# Revit family: 859-000X-001 DN350-600
name_source: partatom
category: Pipe Accessories
units: mm (PartAtom-declared; Revit-internal decimal feet)

## family parameters
Always vertical = Yes
Cut with Voids When Loaded = No
Part Type = Valve - Breaks Into
Round Connector Dimension = Use Diameter
Shared = No
Work Plane-Based = No

## types (34) — shared parameters
10 = 10 mm  [stored 0.0328084 ft]
18 = 11 mm  [stored 0.0360892 ft]
3 = 3 mm  [stored 0.00984252 ft]
50 = 50 mm
8 = 8 mm  [stored 0.0262467 ft]
DN350_PN10 Pilot range ( 0.1 - 1) = 859-0350-00-0140003
DN350_PN10 Pilot range ( 0.6 - 6) = 859-0350-00-0140000
DN350_PN10 Pilot range ( 5 - 10) = 859-0350-00-0140001
DN350_PN16 Pilot range ( 0.1 - 1) = 859-0350-00-1140003
DN350_PN16 Pilot range ( 0.6 - 6) = 859-0350-00-1140000
DN350_PN16 Pilot range ( 10 - 16) = 859-0350-00-1140002
DN350_PN16 Pilot range ( 5 - 10) = 859-0350-00-1140001
DN400_PN10 Pilot range ( 0.1 - 1) = 859-0400-00-0140003
DN400_PN10 Pilot range ( 0.6 - 6) = 859-0400-00-0140000
DN400_PN10 Pilot range ( 5 - 10) = 859-0400-00-0140001
DN400_PN16 Pilot range ( 0.1 - 1) = 859-0400-00-1140003
DN400_PN16 Pilot range ( 0.6 - 6) = 859-0400-00-1140000
DN400_PN16 Pilot range ( 10 - 16) = 859-0400-00-1140002
DN400_PN16 Pilot range ( 5 - 10) = 859-0400-00-1140001
DN450_PN10 Pilot range ( 0.1 - 1) = 859-0450-00-0140003
DN450_PN10 Pilot range ( 0.6 - 6) = 859-0450-00-0140000
DN450_PN10 Pilot range ( 5 - 10) = 859-0450-00-0140001
DN450_PN16 Pilot range (  0.1 - 1) = 859-0450-00-1140003
DN450_PN16 Pilot range ( 10 - 16) = 859-0450-00-1140002
DN450_PN16 Pilot range ( 5 - 10) = 859-0450-00-1140001
DN500_PN10 Pilot range ( 0.1 - 1) = 859-0500-00-0140003
DN500_PN10 Pilot range ( 0.6 - 6) = 859-0500-00-0140000
DN500_PN10 Pilot range ( 5 - 10) = 859-0500-00-0140001
DN500_PN16 Pilot range ( 0.1 - 1) = 859-0500-00-1140003
DN500_PN16 Pilot range ( 0.6 - 6) = 859-0500-00-1140000
DN500_PN16 Pilot range ( 10 - 16) = 859-0500-00-1140002
DN500_PN16 Pilot range ( 5 - 10) = 859-0500-00-1140001
DN600_PN10 Pilot range ( 0.1 - 1) = 859-0600-00-0140003
DN600_PN10 Pilot range ( 0.6 - 6) = 859-0600-00-0140000
DN600_PN10 Pilot range ( 5 - 10) = 859-0600-00-0140001
DN600_PN16 Pilot range ( 0.1 - 1) = 859-0600-00-1140003
DN600_PN16 Pilot range ( 0.6 - 6) = 859-0600-00-1140000
DN600_PN16 Pilot range ( 10 - 16) = 859-0600-00-1140002
DN600_PN16 Pilot range ( 5 - 10) = 859-0600-00-1140001
Description_ = AVK CONTROL VALVE, PRESSURE REDUCING, PN10/16
Search_table = 859-000X-001 DN350-600
URL_product_pages = https://www.avkvalves.com
zero-valued in all types: 0, Default Elevation, Nut_Dim_T

## per-type parameters (varying)
- DN350_PN10 Pilot range ( 0.6 - 6): Actuator_L=136 mm; Actuator_L1=122 mm; Actuator_d=49 mm; Body_H=282 mm; Body_Rib_L=118 mm; Bolt_Dia=33 mm; Bonnet_D=141 mm; Bonnet_D1=282 mm; Bonnet_R=296 mm; Bonnet_dim1=197 mm; Bonnet_dim1_H=41 mm; Bonnet_dim1_H1=400 mm; Bonnet_dim2=99 mm; Bonnet_dim3=74 mm; Bore=175 mm; Bore1=210 mm; Bore2=200 mm; Bore22=220 mm; Centre_D=70 mm; Centre_D1=56 mm; Centre_nut=53 mm; Control_dim1=19 mm  [stored 0.062336 ft]; Control_dim2=89 mm; Control_dim3=9 mm  [stored 0.0295276 ft]; Control_dim4=254 mm; Control_dim5=25 mm  [stored 0.082021 ft]; Control_dim6=30 mm  [stored 0.0984252 ft]; Control_dim7=40 mm  [stored 0.131234 ft]; D=235 mm; DN=350 mm; FL_T=25 mm  [stored 0.082021 ft]; H3=794 mm; H33=48 mm; H4=96 mm; L=980 mm; L3=326 mm; Nut_Dim1=42 mm; Nut_Dim2=7 mm  [stored 0.0229659 ft]; Nut_T=16 mm; Raised_R=24 mm  [stored 0.0787402 ft]; Raised_dis=4 mm  [stored 0.0131234 ft]; Sweep_R=19 mm  [stored 0.062336 ft]; Thickness=15 mm  [stored 0.0492126 ft]; Thickness1=18 mm  [stored 0.0590551 ft]; W=290 mm; W1=302 mm; W11=249 mm; W2=302 mm; W22=196 mm; bore2=200 mm; centre=273 mm; dim1=60 mm; dim2=151 mm; nut_dim=141 mm; sweep=30 mm  [stored 0.0984252 ft]; sweep/2=6 mm  [stored 0.019685 ft]; sweep1=13 mm  [stored 0.0426509 ft]; sweep_D=25 mm  [stored 0.082021 ft]; sweep_H=363 mm; sweep_H1=57 mm; sweep_box1=28 mm  [stored 0.0918635 ft]; sweep_box2=16 mm
- DN350_PN10 Pilot range ( 5 - 10): Actuator_L=136 mm; Actuator_L1=122 mm; Actuator_d=49 mm; Body_H=282 mm; Body_Rib_L=118 mm; Bolt_Dia=33 mm; Bonnet_D=141 mm; Bonnet_D1=282 mm; Bonnet_R=296 mm; Bonnet_dim1=197 mm; Bonnet_dim1_H=41 mm; Bonnet_dim1_H1=400 mm; Bonnet_dim2=99 mm; Bonnet_dim3=74 mm; Bore=175 mm; Bore1=210 mm; Bore2=200 mm; Bore22=220 mm; Centre_D=70 mm; Centre_D1=56 mm; Centre_nut=53 mm; Control_dim1=19 mm  [stored 0.062336 ft]; Control_dim2=89 mm; Control_dim3=9 mm  [stored 0.0295276 ft]; Control_dim4=254 mm; Control_dim5=25 mm  [stored 0.082021 ft]; Control_dim6=30 mm  [stored 0.0984252 ft]; Control_dim7=40 mm  [stored 0.131234 ft]; D=235 mm; DN=350 mm; FL_T=25 mm  [stored 0.082021 ft]; H3=794 mm; H33=48 mm; H4=96 mm; L=980 mm; L3=326 mm; Nut_Dim1=42 mm; Nut_Dim2=7 mm  [stored 0.0229659 ft]; Nut_T=16 mm; Raised_R=24 mm  [stored 0.0787402 ft]; Raised_dis=4 mm  [stored 0.0131234 ft]; Sweep_R=19 mm  [stored 0.062336 ft]; Thickness=15 mm  [stored 0.0492126 ft]; Thickness1=18 mm  [stored 0.0590551 ft]; W=290 mm; W1=302 mm; W11=249 mm; W2=302 mm; W22=196 mm; bore2=200 mm; centre=273 mm; dim1=60 mm; dim2=151 mm; nut_dim=141 mm; sweep=30 mm  [stored 0.0984252 ft]; sweep/2=6 mm  [stored 0.019685 ft]; sweep1=13 mm  [stored 0.0426509 ft]; sweep_D=25 mm  [stored 0.082021 ft]; sweep_H=363 mm; sweep_H1=57 mm; sweep_box1=28 mm  [stored 0.0918635 ft]; sweep_box2=16 mm
- DN350_PN10 Pilot range ( 0.1 - 1): Actuator_L=136 mm; Actuator_L1=122 mm; Actuator_d=49 mm; Body_H=282 mm; Body_Rib_L=118 mm; Bolt_Dia=33 mm; Bonnet_D=141 mm; Bonnet_D1=282 mm; Bonnet_R=296 mm; Bonnet_dim1=197 mm; Bonnet_dim1_H=41 mm; Bonnet_dim1_H1=400 mm; Bonnet_dim2=99 mm; Bonnet_dim3=74 mm; Bore=175 mm; Bore1=210 mm; Bore2=200 mm; Bore22=220 mm; Centre_D=70 mm; Centre_D1=56 mm; Centre_nut=53 mm; Control_dim1=19 mm  [stored 0.062336 ft]; Control_dim2=89 mm; Control_dim3=9 mm  [stored 0.0295276 ft]; Control_dim4=254 mm; Control_dim5=25 mm  [stored 0.082021 ft]; Control_dim6=30 mm  [stored 0.0984252 ft]; Control_dim7=40 mm  [stored 0.131234 ft]; D=235 mm; DN=350 mm; FL_T=25 mm  [stored 0.082021 ft]; H3=794 mm; H33=48 mm; H4=96 mm; L=980 mm; L3=326 mm; Nut_Dim1=42 mm; Nut_Dim2=7 mm  [stored 0.0229659 ft]; Nut_T=16 mm; Raised_R=24 mm  [stored 0.0787402 ft]; Raised_dis=4 mm  [stored 0.0131234 ft]; Sweep_R=19 mm  [stored 0.062336 ft]; Thickness=15 mm  [stored 0.0492126 ft]; Thickness1=18 mm  [stored 0.0590551 ft]; W=290 mm; W1=302 mm; W11=249 mm; W2=302 mm; W22=196 mm; bore2=200 mm; centre=273 mm; dim1=60 mm; dim2=151 mm; nut_dim=141 mm; sweep=30 mm  [stored 0.0984252 ft]; sweep/2=6 mm  [stored 0.019685 ft]; sweep1=13 mm  [stored 0.0426509 ft]; sweep_D=25 mm  [stored 0.082021 ft]; sweep_H=363 mm; sweep_H1=57 mm; sweep_box1=28 mm  [stored 0.0918635 ft]; sweep_box2=16 mm
- DN350_PN16 Pilot range ( 0.6 - 6): Actuator_L=136 mm; Actuator_L1=122 mm; Actuator_d=49 mm; Body_H=282 mm; Body_Rib_L=118 mm; Bolt_Dia=33 mm; Bonnet_D=141 mm; Bonnet_D1=282 mm; Bonnet_R=296 mm; Bonnet_dim1=197 mm; Bonnet_dim1_H=41 mm; Bonnet_dim1_H1=400 mm; Bonnet_dim2=99 mm; Bonnet_dim3=74 mm; Bore=175 mm; Bore1=210 mm; Bore2=200 mm; Bore22=220 mm; Centre_D=70 mm; Centre_D1=56 mm; Centre_nut=53 mm; Control_dim1=19 mm  [stored 0.062336 ft]; Control_dim2=89 mm; Control_dim3=9 mm  [stored 0.0295276 ft]; Control_dim4=254 mm; Control_dim5=25 mm  [stored 0.082021 ft]; Control_dim6=30 mm  [stored 0.0984252 ft]; Control_dim7=40 mm  [stored 0.131234 ft]; D=235 mm; DN=350 mm; FL_T=25 mm  [stored 0.082021 ft]; H3=794 mm; H33=48 mm; H4=96 mm; L=980 mm; L3=326 mm; Nut_Dim1=42 mm; Nut_Dim2=7 mm  [stored 0.0229659 ft]; Nut_T=16 mm; Raised_R=24 mm  [stored 0.0787402 ft]; Raised_dis=4 mm  [stored 0.0131234 ft]; Sweep_R=19 mm  [stored 0.062336 ft]; Thickness=15 mm  [stored 0.0492126 ft]; Thickness1=18 mm  [stored 0.0590551 ft]; W=290 mm; W1=302 mm; W11=249 mm; W2=302 mm; W22=196 mm; bore2=200 mm; centre=273 mm; dim1=60 mm; dim2=151 mm; nut_dim=141 mm; sweep=30 mm  [stored 0.0984252 ft]; sweep/2=6 mm  [stored 0.019685 ft]; sweep1=13 mm  [stored 0.0426509 ft]; sweep_D=25 mm  [stored 0.082021 ft]; sweep_H=363 mm; sweep_H1=57 mm; sweep_box1=28 mm  [stored 0.0918635 ft]; sweep_box2=16 mm
- DN350_PN16 Pilot range ( 5 - 10): Actuator_L=136 mm; Actuator_L1=122 mm; Actuator_d=49 mm; Body_H=282 mm; Body_Rib_L=118 mm; Bolt_Dia=33 mm; Bonnet_D=141 mm; Bonnet_D1=282 mm; Bonnet_R=296 mm; Bonnet_dim1=197 mm; Bonnet_dim1_H=41 mm; Bonnet_dim1_H1=400 mm; Bonnet_dim2=99 mm; Bonnet_dim3=74 mm; Bore=175 mm; Bore1=210 mm; Bore2=200 mm; Bore22=220 mm; Centre_D=70 mm; Centre_D1=56 mm; Centre_nut=53 mm; Control_dim1=19 mm  [stored 0.062336 ft]; Control_dim2=89 mm; Control_dim3=9 mm  [stored 0.0295276 ft]; Control_dim4=254 mm; Control_dim5=25 mm  [stored 0.082021 ft]; Control_dim6=30 mm  [stored 0.0984252 ft]; Control_dim7=40 mm  [stored 0.131234 ft]; D=235 mm; DN=350 mm; FL_T=25 mm  [stored 0.082021 ft]; H3=794 mm; H33=48 mm; H4=96 mm; L=980 mm; L3=326 mm; Nut_Dim1=42 mm; Nut_Dim2=7 mm  [stored 0.0229659 ft]; Nut_T=16 mm; Raised_R=24 mm  [stored 0.0787402 ft]; Raised_dis=4 mm  [stored 0.0131234 ft]; Sweep_R=19 mm  [stored 0.062336 ft]; Thickness=15 mm  [stored 0.0492126 ft]; Thickness1=18 mm  [stored 0.0590551 ft]; W=290 mm; W1=302 mm; W11=249 mm; W2=302 mm; W22=196 mm; bore2=200 mm; centre=273 mm; dim1=60 mm; dim2=151 mm; nut_dim=141 mm; sweep=30 mm  [stored 0.0984252 ft]; sweep/2=6 mm  [stored 0.019685 ft]; sweep1=13 mm  [stored 0.0426509 ft]; sweep_D=25 mm  [stored 0.082021 ft]; sweep_H=363 mm; sweep_H1=57 mm; sweep_box1=28 mm  [stored 0.0918635 ft]; sweep_box2=16 mm
- DN350_PN16 Pilot range ( 10 - 16): Actuator_L=136 mm; Actuator_L1=122 mm; Actuator_d=49 mm; Body_H=282 mm; Body_Rib_L=118 mm; Bolt_Dia=33 mm; Bonnet_D=141 mm; Bonnet_D1=282 mm; Bonnet_R=296 mm; Bonnet_dim1=197 mm; Bonnet_dim1_H=41 mm; Bonnet_dim1_H1=400 mm; Bonnet_dim2=99 mm; Bonnet_dim3=74 mm; Bore=175 mm; Bore1=210 mm; Bore2=200 mm; Bore22=220 mm; Centre_D=70 mm; Centre_D1=56 mm; Centre_nut=53 mm; Control_dim1=19 mm  [stored 0.062336 ft]; Control_dim2=89 mm; Control_dim3=9 mm  [stored 0.0295276 ft]; Control_dim4=254 mm; Control_dim5=25 mm  [stored 0.082021 ft]; Control_dim6=30 mm  [stored 0.0984252 ft]; Control_dim7=40 mm  [stored 0.131234 ft]; D=235 mm; DN=350 mm; FL_T=25 mm  [stored 0.082021 ft]; H3=794 mm; H33=48 mm; H4=96 mm; L=980 mm; L3=326 mm; Nut_Dim1=42 mm; Nut_Dim2=7 mm  [stored 0.0229659 ft]; Nut_T=16 mm; Raised_R=24 mm  [stored 0.0787402 ft]; Raised_dis=4 mm  [stored 0.0131234 ft]; Sweep_R=19 mm  [stored 0.062336 ft]; Thickness=15 mm  [stored 0.0492126 ft]; Thickness1=18 mm  [stored 0.0590551 ft]; W=290 mm; W1=302 mm; W11=249 mm; W2=302 mm; W22=196 mm; bore2=200 mm; centre=273 mm; dim1=60 mm; dim2=151 mm; nut_dim=141 mm; sweep=30 mm  [stored 0.0984252 ft]; sweep/2=6 mm  [stored 0.019685 ft]; sweep1=13 mm  [stored 0.0426509 ft]; sweep_D=25 mm  [stored 0.082021 ft]; sweep_H=363 mm; sweep_H1=57 mm; sweep_box1=28 mm  [stored 0.0918635 ft]; sweep_box2=16 mm
- DN350_PN16 Pilot range ( 0.1 - 1): Actuator_L=136 mm; Actuator_L1=122 mm; Actuator_d=49 mm; Body_H=282 mm; Body_Rib_L=118 mm; Bolt_Dia=33 mm; Bonnet_D=141 mm; Bonnet_D1=282 mm; Bonnet_R=296 mm; Bonnet_dim1=197 mm; Bonnet_dim1_H=41 mm; Bonnet_dim1_H1=400 mm; Bonnet_dim2=99 mm; Bonnet_dim3=74 mm; Bore=175 mm; Bore1=210 mm; Bore2=200 mm; Bore22=220 mm; Centre_D=70 mm; Centre_D1=56 mm; Centre_nut=53 mm; Control_dim1=19 mm  [stored 0.062336 ft]; Control_dim2=89 mm; Control_dim3=9 mm  [stored 0.0295276 ft]; Control_dim4=254 mm; Control_dim5=25 mm  [stored 0.082021 ft]; Control_dim6=30 mm  [stored 0.0984252 ft]; Control_dim7=40 mm  [stored 0.131234 ft]; D=235 mm; DN=350 mm; FL_T=25 mm  [stored 0.082021 ft]; H3=794 mm; H33=48 mm; H4=96 mm; L=980 mm; L3=326 mm; Nut_Dim1=42 mm; Nut_Dim2=7 mm  [stored 0.0229659 ft]; Nut_T=16 mm; Raised_R=24 mm  [stored 0.0787402 ft]; Raised_dis=4 mm  [stored 0.0131234 ft]; Sweep_R=19 mm  [stored 0.062336 ft]; Thickness=15 mm  [stored 0.0492126 ft]; Thickness1=18 mm  [stored 0.0590551 ft]; W=290 mm; W1=302 mm; W11=249 mm; W2=302 mm; W22=196 mm; bore2=200 mm; centre=273 mm; dim1=60 mm; dim2=151 mm; nut_dim=141 mm; sweep=30 mm  [stored 0.0984252 ft]; sweep/2=6 mm  [stored 0.019685 ft]; sweep1=13 mm  [stored 0.0426509 ft]; sweep_D=25 mm  [stored 0.082021 ft]; sweep_H=363 mm; sweep_H1=57 mm; sweep_box1=28 mm  [stored 0.0918635 ft]; sweep_box2=16 mm
- DN400_PN10 Pilot range ( 0.6 - 6): Actuator_L=154 mm; Actuator_L1=139 mm; Actuator_d=54 mm; Body_H=315 mm; Body_Rib_L=131 mm; Bolt_Dia=39 mm  [stored 0.127953 ft]; Bonnet_D=158 mm; Bonnet_D1=315 mm; Bonnet_R=331 mm; Bonnet_dim1=221 mm; Bonnet_dim1_H=53 mm; Bonnet_dim1_H1=463 mm; Bonnet_dim2=110 mm; Bonnet_dim3=83 mm; Bore=200 mm; Bore1=240 mm; Bore2=223 mm; Bore22=245 mm; Centre_D=80 mm; Centre_D1=64 mm; Centre_nut=60 mm; Control_dim1=21 mm  [stored 0.0688976 ft]; Control_dim2=99 mm; Control_dim3=10 mm  [stored 0.0328084 ft]; Control_dim4=284 mm; Control_dim5=28 mm  [stored 0.0918635 ft]; Control_dim6=33 mm; Control_dim7=45 mm  [stored 0.147638 ft]; D=263 mm; DN=400 mm; FL_T=25 mm  [stored 0.082021 ft]; H3=910 mm; H33=55 mm; H4=111 mm; L=1100 mm; L3=364 mm; Nut_Dim1=51 mm; Nut_Dim2=8 mm  [stored 0.0262467 ft]; Nut_T=16 mm; Raised_R=25 mm  [stored 0.082021 ft]; Raised_dis=4 mm  [stored 0.0131234 ft]; Sweep_R=23 mm; Thickness=15 mm  [stored 0.0492126 ft]; Thickness1=18 mm  [stored 0.0590551 ft]; W=328 mm; W1=343 mm; W11=281 mm; W2=343 mm; W22=223 mm; bore2=223 mm; centre=312 mm; dim1=69 mm; dim2=171 mm; nut_dim=158 mm; sweep=36 mm  [stored 0.11811 ft]; sweep/2=8 mm  [stored 0.0262467 ft]; sweep1=15 mm  [stored 0.0492126 ft]; sweep_D=30 mm  [stored 0.0984252 ft]; sweep_H=421 mm; sweep_H1=74 mm; sweep_box1=32 mm  [stored 0.104987 ft]; sweep_box2=20 mm  [stored 0.0656168 ft]
- DN400_PN10 Pilot range ( 5 - 10): Actuator_L=154 mm; Actuator_L1=139 mm; Actuator_d=54 mm; Body_H=315 mm; Body_Rib_L=131 mm; Bolt_Dia=39 mm  [stored 0.127953 ft]; Bonnet_D=158 mm; Bonnet_D1=315 mm; Bonnet_R=331 mm; Bonnet_dim1=221 mm; Bonnet_dim1_H=53 mm; Bonnet_dim1_H1=463 mm; Bonnet_dim2=110 mm; Bonnet_dim3=83 mm; Bore=200 mm; Bore1=240 mm; Bore2=223 mm; Bore22=245 mm; Centre_D=80 mm; Centre_D1=64 mm; Centre_nut=60 mm; Control_dim1=21 mm  [stored 0.0688976 ft]; Control_dim2=99 mm; Control_dim3=10 mm  [stored 0.0328084 ft]; Control_dim4=284 mm; Control_dim5=28 mm  [stored 0.0918635 ft]; Control_dim6=33 mm; Control_dim7=45 mm  [stored 0.147638 ft]; D=263 mm; DN=400 mm; FL_T=25 mm  [stored 0.082021 ft]; H3=910 mm; H33=55 mm; H4=111 mm; L=1100 mm; L3=364 mm; Nut_Dim1=51 mm; Nut_Dim2=8 mm  [stored 0.0262467 ft]; Nut_T=16 mm; Raised_R=25 mm  [stored 0.082021 ft]; Raised_dis=4 mm  [stored 0.0131234 ft]; Sweep_R=23 mm; Thickness=15 mm  [stored 0.0492126 ft]; Thickness1=18 mm  [stored 0.0590551 ft]; W=328 mm; W1=343 mm; W11=281 mm; W2=343 mm; W22=223 mm; bore2=223 mm; centre=312 mm; dim1=69 mm; dim2=171 mm; nut_dim=158 mm; sweep=36 mm  [stored 0.11811 ft]; sweep/2=8 mm  [stored 0.0262467 ft]; sweep1=15 mm  [stored 0.0492126 ft]; sweep_D=30 mm  [stored 0.0984252 ft]; sweep_H=421 mm; sweep_H1=74 mm; sweep_box1=32 mm  [stored 0.104987 ft]; sweep_box2=20 mm  [stored 0.0656168 ft]
- DN400_PN10 Pilot range ( 0.1 - 1): Actuator_L=154 mm; Actuator_L1=139 mm; Actuator_d=54 mm; Body_H=315 mm; Body_Rib_L=131 mm; Bolt_Dia=39 mm  [stored 0.127953 ft]; Bonnet_D=158 mm; Bonnet_D1=315 mm; Bonnet_R=331 mm; Bonnet_dim1=221 mm; Bonnet_dim1_H=53 mm; Bonnet_dim1_H1=463 mm; Bonnet_dim2=110 mm; Bonnet_dim3=83 mm; Bore=200 mm; Bore1=240 mm; Bore2=223 mm; Bore22=245 mm; Centre_D=80 mm; Centre_D1=64 mm; Centre_nut=60 mm; Control_dim1=21 mm  [stored 0.0688976 ft]; Control_dim2=99 mm; Control_dim3=10 mm  [stored 0.0328084 ft]; Control_dim4=284 mm; Control_dim5=28 mm  [stored 0.0918635 ft]; Control_dim6=33 mm; Control_dim7=45 mm  [stored 0.147638 ft]; D=263 mm; DN=400 mm; FL_T=25 mm  [stored 0.082021 ft]; H3=910 mm; H33=55 mm; H4=111 mm; L=1100 mm; L3=364 mm; Nut_Dim1=51 mm; Nut_Dim2=8 mm  [stored 0.0262467 ft]; Nut_T=16 mm; Raised_R=25 mm  [stored 0.082021 ft]; Raised_dis=4 mm  [stored 0.0131234 ft]; Sweep_R=23 mm; Thickness=15 mm  [stored 0.0492126 ft]; Thickness1=18 mm  [stored 0.0590551 ft]; W=328 mm; W1=343 mm; W11=281 mm; W2=343 mm; W22=223 mm; bore2=223 mm; centre=312 mm; dim1=69 mm; dim2=171 mm; nut_dim=158 mm; sweep=36 mm  [stored 0.11811 ft]; sweep/2=8 mm  [stored 0.0262467 ft]; sweep1=15 mm  [stored 0.0492126 ft]; sweep_D=30 mm  [stored 0.0984252 ft]; sweep_H=421 mm; sweep_H1=74 mm; sweep_box1=32 mm  [stored 0.104987 ft]; sweep_box2=20 mm  [stored 0.0656168 ft]
- DN400_PN16 Pilot range ( 0.6 - 6): Actuator_L=154 mm; Actuator_L1=139 mm; Actuator_d=54 mm; Body_H=315 mm; Body_Rib_L=131 mm; Bolt_Dia=39 mm  [stored 0.127953 ft]; Bonnet_D=158 mm; Bonnet_D1=315 mm; Bonnet_R=331 mm; Bonnet_dim1=221 mm; Bonnet_dim1_H=53 mm; Bonnet_dim1_H1=463 mm; Bonnet_dim2=110 mm; Bonnet_dim3=83 mm; Bore=200 mm; Bore1=240 mm; Bore2=223 mm; Bore22=245 mm; Centre_D=80 mm; Centre_D1=64 mm; Centre_nut=60 mm; Control_dim1=21 mm  [stored 0.0688976 ft]; Control_dim2=99 mm; Control_dim3=10 mm  [stored 0.0328084 ft]; Control_dim4=284 mm; Control_dim5=28 mm  [stored 0.0918635 ft]; Control_dim6=33 mm; Control_dim7=45 mm  [stored 0.147638 ft]; D=263 mm; DN=400 mm; FL_T=25 mm  [stored 0.082021 ft]; H3=910 mm; H33=55 mm; H4=111 mm; L=1100 mm; L3=364 mm; Nut_Dim1=51 mm; Nut_Dim2=8 mm  [stored 0.0262467 ft]; Nut_T=16 mm; Raised_R=25 mm  [stored 0.082021 ft]; Raised_dis=4 mm  [stored 0.0131234 ft]; Sweep_R=23 mm; Thickness=15 mm  [stored 0.0492126 ft]; Thickness1=18 mm  [stored 0.0590551 ft]; W=328 mm; W1=343 mm; W11=281 mm; W2=343 mm; W22=223 mm; bore2=223 mm; centre=312 mm; dim1=69 mm; dim2=171 mm; nut_dim=158 mm; sweep=36 mm  [stored 0.11811 ft]; sweep/2=8 mm  [stored 0.0262467 ft]; sweep1=15 mm  [stored 0.0492126 ft]; sweep_D=30 mm  [stored 0.0984252 ft]; sweep_H=421 mm; sweep_H1=74 mm; sweep_box1=32 mm  [stored 0.104987 ft]; sweep_box2=20 mm  [stored 0.0656168 ft]
- DN400_PN16 Pilot range ( 5 - 10): Actuator_L=154 mm; Actuator_L1=139 mm; Actuator_d=54 mm; Body_H=315 mm; Body_Rib_L=131 mm; Bolt_Dia=39 mm  [stored 0.127953 ft]; Bonnet_D=158 mm; Bonnet_D1=315 mm; Bonnet_R=331 mm; Bonnet_dim1=221 mm; Bonnet_dim1_H=53 mm; Bonnet_dim1_H1=463 mm; Bonnet_dim2=110 mm; Bonnet_dim3=83 mm; Bore=200 mm; Bore1=240 mm; Bore2=223 mm; Bore22=245 mm; Centre_D=80 mm; Centre_D1=64 mm; Centre_nut=60 mm; Control_dim1=21 mm  [stored 0.0688976 ft]; Control_dim2=99 mm; Control_dim3=10 mm  [stored 0.0328084 ft]; Control_dim4=284 mm; Control_dim5=28 mm  [stored 0.0918635 ft]; Control_dim6=33 mm; Control_dim7=45 mm  [stored 0.147638 ft]; D=263 mm; DN=400 mm; FL_T=25 mm  [stored 0.082021 ft]; H3=910 mm; H33=55 mm; H4=111 mm; L=1100 mm; L3=364 mm; Nut_Dim1=51 mm; Nut_Dim2=8 mm  [stored 0.0262467 ft]; Nut_T=16 mm; Raised_R=25 mm  [stored 0.082021 ft]; Raised_dis=4 mm  [stored 0.0131234 ft]; Sweep_R=23 mm; Thickness=15 mm  [stored 0.0492126 ft]; Thickness1=18 mm  [stored 0.0590551 ft]; W=328 mm; W1=343 mm; W11=281 mm; W2=343 mm; W22=223 mm; bore2=223 mm; centre=312 mm; dim1=69 mm; dim2=171 mm; nut_dim=158 mm; sweep=36 mm  [stored 0.11811 ft]; sweep/2=8 mm  [stored 0.0262467 ft]; sweep1=15 mm  [stored 0.0492126 ft]; sweep_D=30 mm  [stored 0.0984252 ft]; sweep_H=421 mm; sweep_H1=74 mm; sweep_box1=32 mm  [stored 0.104987 ft]; sweep_box2=20 mm  [stored 0.0656168 ft]
- DN400_PN16 Pilot range ( 10 - 16): Actuator_L=154 mm; Actuator_L1=139 mm; Actuator_d=54 mm; Body_H=315 mm; Body_Rib_L=131 mm; Bolt_Dia=39 mm  [stored 0.127953 ft]; Bonnet_D=158 mm; Bonnet_D1=315 mm; Bonnet_R=331 mm; Bonnet_dim1=221 mm; Bonnet_dim1_H=53 mm; Bonnet_dim1_H1=463 mm; Bonnet_dim2=110 mm; Bonnet_dim3=83 mm; Bore=200 mm; Bore1=240 mm; Bore2=223 mm; Bore22=245 mm; Centre_D=80 mm; Centre_D1=64 mm; Centre_nut=60 mm; Control_dim1=21 mm  [stored 0.0688976 ft]; Control_dim2=99 mm; Control_dim3=10 mm  [stored 0.0328084 ft]; Control_dim4=284 mm; Control_dim5=28 mm  [stored 0.0918635 ft]; Control_dim6=33 mm; Control_dim7=45 mm  [stored 0.147638 ft]; D=263 mm; DN=400 mm; FL_T=25 mm  [stored 0.082021 ft]; H3=910 mm; H33=55 mm; H4=111 mm; L=1100 mm; L3=364 mm; Nut_Dim1=51 mm; Nut_Dim2=8 mm  [stored 0.0262467 ft]; Nut_T=16 mm; Raised_R=25 mm  [stored 0.082021 ft]; Raised_dis=4 mm  [stored 0.0131234 ft]; Sweep_R=23 mm; Thickness=15 mm  [stored 0.0492126 ft]; Thickness1=18 mm  [stored 0.0590551 ft]; W=328 mm; W1=343 mm; W11=281 mm; W2=343 mm; W22=223 mm; bore2=223 mm; centre=312 mm; dim1=69 mm; dim2=171 mm; nut_dim=158 mm; sweep=36 mm  [stored 0.11811 ft]; sweep/2=8 mm  [stored 0.0262467 ft]; sweep1=15 mm  [stored 0.0492126 ft]; sweep_D=30 mm  [stored 0.0984252 ft]; sweep_H=421 mm; sweep_H1=74 mm; sweep_box1=32 mm  [stored 0.104987 ft]; sweep_box2=20 mm  [stored 0.0656168 ft]
- DN400_PN16 Pilot range ( 0.1 - 1): Actuator_L=154 mm; Actuator_L1=139 mm; Actuator_d=54 mm; Body_H=315 mm; Body_Rib_L=131 mm; Bolt_Dia=39 mm  [stored 0.127953 ft]; Bonnet_D=158 mm; Bonnet_D1=315 mm; Bonnet_R=331 mm; Bonnet_dim1=221 mm; Bonnet_dim1_H=53 mm; Bonnet_dim1_H1=463 mm; Bonnet_dim2=110 mm; Bonnet_dim3=83 mm; Bore=200 mm; Bore1=240 mm; Bore2=223 mm; Bore22=245 mm; Centre_D=80 mm; Centre_D1=64 mm; Centre_nut=60 mm; Control_dim1=21 mm  [stored 0.0688976 ft]; Control_dim2=99 mm; Control_dim3=10 mm  [stored 0.0328084 ft]; Control_dim4=284 mm; Control_dim5=28 mm  [stored 0.0918635 ft]; Control_dim6=33 mm; Control_dim7=45 mm  [stored 0.147638 ft]; D=263 mm; DN=400 mm; FL_T=25 mm  [stored 0.082021 ft]; H3=910 mm; H33=55 mm; H4=111 mm; L=1100 mm; L3=364 mm; Nut_Dim1=51 mm; Nut_Dim2=8 mm  [stored 0.0262467 ft]; Nut_T=16 mm; Raised_R=25 mm  [stored 0.082021 ft]; Raised_dis=4 mm  [stored 0.0131234 ft]; Sweep_R=23 mm; Thickness=15 mm  [stored 0.0492126 ft]; Thickness1=18 mm  [stored 0.0590551 ft]; W=328 mm; W1=343 mm; W11=281 mm; W2=343 mm; W22=223 mm; bore2=223 mm; centre=312 mm; dim1=69 mm; dim2=171 mm; nut_dim=158 mm; sweep=36 mm  [stored 0.11811 ft]; sweep/2=8 mm  [stored 0.0262467 ft]; sweep1=15 mm  [stored 0.0492126 ft]; sweep_D=30 mm  [stored 0.0984252 ft]; sweep_H=421 mm; sweep_H1=74 mm; sweep_box1=32 mm  [stored 0.104987 ft]; sweep_box2=20 mm  [stored 0.0656168 ft]
- DN450_PN10 Pilot range ( 0.6 - 6): Actuator_L=179 mm; Actuator_L1=161 mm; Actuator_d=60 mm; Body_H=351 mm; Body_Rib_L=146 mm; Bolt_Dia=39 mm  [stored 0.127953 ft]; Bonnet_D=176 mm; Bonnet_D1=351 mm; Bonnet_R=369 mm; Bonnet_dim1=246 mm; Bonnet_dim1_H=47 mm; Bonnet_dim1_H1=490 mm; Bonnet_dim2=123 mm; Bonnet_dim3=92 mm; Bore=225 mm; Bore1=270 mm; Bore2=249 mm; Bore22=273 mm; Centre_D=90 mm; Centre_D1=72 mm; Centre_nut=68 mm; Control_dim1=23 mm; Control_dim2=111 mm; Control_dim3=12 mm  [stored 0.0393701 ft]; Control_dim4=316 mm; Control_dim5=31 mm; Control_dim6=37 mm; Control_dim7=50 mm; D=293 mm; DN=450 mm; FL_T=26 mm; H3=978 mm; H33=59 mm; H4=117 mm; L=1200 mm; L3=405 mm; Nut_Dim1=51 mm; Nut_Dim2=9 mm  [stored 0.0295276 ft]; Nut_T=17 mm; Raised_R=27 mm; Raised_dis=4 mm  [stored 0.0131234 ft]; Sweep_R=23 mm; Thickness=15 mm  [stored 0.0492126 ft]; Thickness1=18 mm  [stored 0.0590551 ft]; W=383 mm; W1=398 mm; W11=331 mm; W2=398 mm; W22=259 mm; bore2=249 mm; centre=351 mm; dim1=80 mm; dim2=199 mm; nut_dim=176 mm; sweep=36 mm  [stored 0.11811 ft]; sweep/2=8 mm  [stored 0.0262467 ft]; sweep1=15 mm  [stored 0.0492126 ft]; sweep_D=30 mm  [stored 0.0984252 ft]; sweep_H=446 mm; sweep_H1=66 mm; sweep_box1=36 mm  [stored 0.11811 ft]; sweep_box2=20 mm  [stored 0.0656168 ft]
- DN450_PN10 Pilot range ( 5 - 10): Actuator_L=179 mm; Actuator_L1=161 mm; Actuator_d=60 mm; Body_H=351 mm; Body_Rib_L=146 mm; Bolt_Dia=39 mm  [stored 0.127953 ft]; Bonnet_D=176 mm; Bonnet_D1=351 mm; Bonnet_R=369 mm; Bonnet_dim1=246 mm; Bonnet_dim1_H=47 mm; Bonnet_dim1_H1=490 mm; Bonnet_dim2=123 mm; Bonnet_dim3=92 mm; Bore=225 mm; Bore1=270 mm; Bore2=249 mm; Bore22=273 mm; Centre_D=90 mm; Centre_D1=72 mm; Centre_nut=68 mm; Control_dim1=23 mm; Control_dim2=111 mm; Control_dim3=12 mm  [stored 0.0393701 ft]; Control_dim4=316 mm; Control_dim5=31 mm; Control_dim6=37 mm; Control_dim7=50 mm; D=293 mm; DN=450 mm; FL_T=26 mm; H3=978 mm; H33=59 mm; H4=117 mm; L=1200 mm; L3=405 mm; Nut_Dim1=51 mm; Nut_Dim2=9 mm  [stored 0.0295276 ft]; Nut_T=17 mm; Raised_R=27 mm; Raised_dis=4 mm  [stored 0.0131234 ft]; Sweep_R=23 mm; Thickness=15 mm  [stored 0.0492126 ft]; Thickness1=18 mm  [stored 0.0590551 ft]; W=383 mm; W1=398 mm; W11=331 mm; W2=398 mm; W22=259 mm; bore2=249 mm; centre=351 mm; dim1=80 mm; dim2=199 mm; nut_dim=176 mm; sweep=36 mm  [stored 0.11811 ft]; sweep/2=8 mm  [stored 0.0262467 ft]; sweep1=15 mm  [stored 0.0492126 ft]; sweep_D=30 mm  [stored 0.0984252 ft]; sweep_H=446 mm; sweep_H1=66 mm; sweep_box1=36 mm  [stored 0.11811 ft]; sweep_box2=20 mm  [stored 0.0656168 ft]
- DN450_PN10 Pilot range ( 0.1 - 1): Actuator_L=179 mm; Actuator_L1=161 mm; Actuator_d=60 mm; Body_H=351 mm; Body_Rib_L=146 mm; Bolt_Dia=39 mm  [stored 0.127953 ft]; Bonnet_D=176 mm; Bonnet_D1=351 mm; Bonnet_R=369 mm; Bonnet_dim1=246 mm; Bonnet_dim1_H=47 mm; Bonnet_dim1_H1=490 mm; Bonnet_dim2=123 mm; Bonnet_dim3=92 mm; Bore=225 mm; Bore1=270 mm; Bore2=249 mm; Bore22=273 mm; Centre_D=90 mm; Centre_D1=72 mm; Centre_nut=68 mm; Control_dim1=23 mm; Control_dim2=111 mm; Control_dim3=12 mm  [stored 0.0393701 ft]; Control_dim4=316 mm; Control_dim5=31 mm; Control_dim6=37 mm; Control_dim7=50 mm; D=293 mm; DN=450 mm; FL_T=26 mm; H3=978 mm; H33=59 mm; H4=117 mm; L=1200 mm; L3=405 mm; Nut_Dim1=51 mm; Nut_Dim2=9 mm  [stored 0.0295276 ft]; Nut_T=17 mm; Raised_R=27 mm; Raised_dis=4 mm  [stored 0.0131234 ft]; Sweep_R=23 mm; Thickness=15 mm  [stored 0.0492126 ft]; Thickness1=18 mm  [stored 0.0590551 ft]; W=383 mm; W1=398 mm; W11=331 mm; W2=398 mm; W22=259 mm; bore2=249 mm; centre=351 mm; dim1=80 mm; dim2=199 mm; nut_dim=176 mm; sweep=36 mm  [stored 0.11811 ft]; sweep/2=8 mm  [stored 0.0262467 ft]; sweep1=15 mm  [stored 0.0492126 ft]; sweep_D=30 mm  [stored 0.0984252 ft]; sweep_H=446 mm; sweep_H1=66 mm; sweep_box1=36 mm  [stored 0.11811 ft]; sweep_box2=20 mm  [stored 0.0656168 ft]
- DN450_PN16 Pilot range ( 5 - 10): Actuator_L=179 mm; Actuator_L1=161 mm; Actuator_d=60 mm; Body_H=351 mm; Body_Rib_L=146 mm; Bolt_Dia=39 mm  [stored 0.127953 ft]; Bonnet_D=176 mm; Bonnet_D1=351 mm; Bonnet_R=369 mm; Bonnet_dim1=246 mm; Bonnet_dim1_H=47 mm; Bonnet_dim1_H1=490 mm; Bonnet_dim2=123 mm; Bonnet_dim3=92 mm; Bore=225 mm; Bore1=270 mm; Bore2=249 mm; Bore22=273 mm; Centre_D=90 mm; Centre_D1=72 mm; Centre_nut=68 mm; Control_dim1=23 mm; Control_dim2=111 mm; Control_dim3=12 mm  [stored 0.0393701 ft]; Control_dim4=316 mm; Control_dim5=31 mm; Control_dim6=37 mm; Control_dim7=50 mm; D=293 mm; DN=450 mm; FL_T=26 mm; H3=978 mm; H33=59 mm; H4=117 mm; L=1200 mm; L3=405 mm; Nut_Dim1=51 mm; Nut_Dim2=9 mm  [stored 0.0295276 ft]; Nut_T=17 mm; Raised_R=27 mm; Raised_dis=4 mm  [stored 0.0131234 ft]; Sweep_R=23 mm; Thickness=15 mm  [stored 0.0492126 ft]; Thickness1=18 mm  [stored 0.0590551 ft]; W=383 mm; W1=398 mm; W11=331 mm; W2=398 mm; W22=259 mm; bore2=249 mm; centre=351 mm; dim1=80 mm; dim2=199 mm; nut_dim=176 mm; sweep=36 mm  [stored 0.11811 ft]; sweep/2=8 mm  [stored 0.0262467 ft]; sweep1=15 mm  [stored 0.0492126 ft]; sweep_D=30 mm  [stored 0.0984252 ft]; sweep_H=446 mm; sweep_H1=66 mm; sweep_box1=36 mm  [stored 0.11811 ft]; sweep_box2=20 mm  [stored 0.0656168 ft]
- DN450_PN16 Pilot range ( 10 - 16): Actuator_L=179 mm; Actuator_L1=161 mm; Actuator_d=60 mm; Body_H=351 mm; Body_Rib_L=146 mm; Bolt_Dia=39 mm  [stored 0.127953 ft]; Bonnet_D=176 mm; Bonnet_D1=351 mm; Bonnet_R=369 mm; Bonnet_dim1=246 mm; Bonnet_dim1_H=47 mm; Bonnet_dim1_H1=490 mm; Bonnet_dim2=123 mm; Bonnet_dim3=92 mm; Bore=225 mm; Bore1=270 mm; Bore2=249 mm; Bore22=273 mm; Centre_D=90 mm; Centre_D1=72 mm; Centre_nut=68 mm; Control_dim1=23 mm; Control_dim2=111 mm; Control_dim3=12 mm  [stored 0.0393701 ft]; Control_dim4=316 mm; Control_dim5=31 mm; Control_dim6=37 mm; Control_dim7=50 mm; D=293 mm; DN=450 mm; FL_T=26 mm; H3=978 mm; H33=59 mm; H4=117 mm; L=1200 mm; L3=405 mm; Nut_Dim1=51 mm; Nut_Dim2=9 mm  [stored 0.0295276 ft]; Nut_T=17 mm; Raised_R=27 mm; Raised_dis=4 mm  [stored 0.0131234 ft]; Sweep_R=23 mm; Thickness=15 mm  [stored 0.0492126 ft]; Thickness1=18 mm  [stored 0.0590551 ft]; W=383 mm; W1=398 mm; W11=331 mm; W2=398 mm; W22=259 mm; bore2=249 mm; centre=351 mm; dim1=80 mm; dim2=199 mm; nut_dim=176 mm; sweep=36 mm  [stored 0.11811 ft]; sweep/2=8 mm  [stored 0.0262467 ft]; sweep1=15 mm  [stored 0.0492126 ft]; sweep_D=30 mm  [stored 0.0984252 ft]; sweep_H=446 mm; sweep_H1=66 mm; sweep_box1=36 mm  [stored 0.11811 ft]; sweep_box2=20 mm  [stored 0.0656168 ft]
- DN450_PN16 Pilot range (  0.1 - 1): Actuator_L=179 mm; Actuator_L1=161 mm; Actuator_d=60 mm; Body_H=351 mm; Body_Rib_L=146 mm; Bolt_Dia=39 mm  [stored 0.127953 ft]; Bonnet_D=176 mm; Bonnet_D1=351 mm; Bonnet_R=369 mm; Bonnet_dim1=246 mm; Bonnet_dim1_H=47 mm; Bonnet_dim1_H1=490 mm; Bonnet_dim2=123 mm; Bonnet_dim3=92 mm; Bore=225 mm; Bore1=270 mm; Bore2=249 mm; Bore22=273 mm; Centre_D=90 mm; Centre_D1=72 mm; Centre_nut=68 mm; Control_dim1=23 mm; Control_dim2=111 mm; Control_dim3=12 mm  [stored 0.0393701 ft]; Control_dim4=316 mm; Control_dim5=31 mm; Control_dim6=37 mm; Control_dim7=50 mm; D=293 mm; DN=450 mm; FL_T=26 mm; H3=978 mm; H33=59 mm; H4=117 mm; L=1200 mm; L3=405 mm; Nut_Dim1=51 mm; Nut_Dim2=9 mm  [stored 0.0295276 ft]; Nut_T=17 mm; Raised_R=27 mm; Raised_dis=4 mm  [stored 0.0131234 ft]; Sweep_R=23 mm; Thickness=15 mm  [stored 0.0492126 ft]; Thickness1=18 mm  [stored 0.0590551 ft]; W=383 mm; W1=398 mm; W11=331 mm; W2=398 mm; W22=259 mm; bore2=249 mm; centre=351 mm; dim1=80 mm; dim2=199 mm; nut_dim=176 mm; sweep=36 mm  [stored 0.11811 ft]; sweep/2=8 mm  [stored 0.0262467 ft]; sweep1=15 mm  [stored 0.0492126 ft]; sweep_D=30 mm  [stored 0.0984252 ft]; sweep_H=446 mm; sweep_H1=66 mm; sweep_box1=36 mm  [stored 0.11811 ft]; sweep_box2=20 mm  [stored 0.0656168 ft]
- DN500_PN10 Pilot range ( 0.6 - 6): Actuator_L=209 mm; Actuator_L1=188 mm; Actuator_d=67 mm; Body_H=390 mm; Body_Rib_L=163 mm; Bolt_Dia=44 mm; Bonnet_D=195 mm; Bonnet_D1=390 mm; Bonnet_R=410 mm; Bonnet_dim1=273 mm; Bonnet_dim1_H=76 mm; Bonnet_dim1_H1=597 mm; Bonnet_dim2=137 mm; Bonnet_dim3=102 mm; Bore=250 mm; Bore1=300 mm; Bore2=276 mm; Bore22=304 mm; Centre_D=100 mm; Centre_D1=80 mm; Centre_nut=75 mm; Control_dim1=26 mm; Control_dim2=123 mm; Control_dim3=13 mm  [stored 0.0426509 ft]; Control_dim4=351 mm; Control_dim5=35 mm  [stored 0.114829 ft]; Control_dim6=41 mm; Control_dim7=56 mm; D=325 mm; DN=500 mm; FL_T=27 mm; H3=1160 mm; H33=71 mm; H4=143 mm; L=1250 mm; L3=450 mm; Nut_Dim1=57 mm; Nut_Dim2=10 mm  [stored 0.0328084 ft]; Nut_T=17 mm; Raised_R=30 mm  [stored 0.0984252 ft]; Raised_dis=4 mm  [stored 0.0131234 ft]; Sweep_R=26 mm; Thickness=16 mm; Thickness1=19 mm  [stored 0.062336 ft]; W=448 mm; W1=465 mm; W11=388 mm; W2=465 mm; W22=302 mm; bore2=276 mm; centre=390 mm; dim1=93 mm; dim2=233 mm; nut_dim=195 mm; sweep=41 mm; sweep/2=9 mm  [stored 0.0295276 ft]; sweep1=17 mm; sweep_D=34 mm  [stored 0.111549 ft]; sweep_H=543 mm; sweep_H1=107 mm; sweep_box1=40 mm  [stored 0.131234 ft]; sweep_box2=22 mm
- DN500_PN10 Pilot range ( 5 - 10): Actuator_L=209 mm; Actuator_L1=188 mm; Actuator_d=67 mm; Body_H=390 mm; Body_Rib_L=163 mm; Bolt_Dia=44 mm; Bonnet_D=195 mm; Bonnet_D1=390 mm; Bonnet_R=410 mm; Bonnet_dim1=273 mm; Bonnet_dim1_H=76 mm; Bonnet_dim1_H1=597 mm; Bonnet_dim2=137 mm; Bonnet_dim3=102 mm; Bore=250 mm; Bore1=300 mm; Bore2=276 mm; Bore22=304 mm; Centre_D=100 mm; Centre_D1=80 mm; Centre_nut=75 mm; Control_dim1=26 mm; Control_dim2=123 mm; Control_dim3=13 mm  [stored 0.0426509 ft]; Control_dim4=351 mm; Control_dim5=35 mm  [stored 0.114829 ft]; Control_dim6=41 mm; Control_dim7=56 mm; D=325 mm; DN=500 mm; FL_T=27 mm; H3=1160 mm; H33=71 mm; H4=143 mm; L=1250 mm; L3=450 mm; Nut_Dim1=57 mm; Nut_Dim2=10 mm  [stored 0.0328084 ft]; Nut_T=17 mm; Raised_R=30 mm  [stored 0.0984252 ft]; Raised_dis=4 mm  [stored 0.0131234 ft]; Sweep_R=26 mm; Thickness=16 mm; Thickness1=19 mm  [stored 0.062336 ft]; W=448 mm; W1=465 mm; W11=388 mm; W2=465 mm; W22=302 mm; bore2=276 mm; centre=390 mm; dim1=93 mm; dim2=233 mm; nut_dim=195 mm; sweep=41 mm; sweep/2=9 mm  [stored 0.0295276 ft]; sweep1=17 mm; sweep_D=34 mm  [stored 0.111549 ft]; sweep_H=543 mm; sweep_H1=107 mm; sweep_box1=40 mm  [stored 0.131234 ft]; sweep_box2=22 mm
- DN500_PN10 Pilot range ( 0.1 - 1): Actuator_L=209 mm; Actuator_L1=188 mm; Actuator_d=67 mm; Body_H=390 mm; Body_Rib_L=163 mm; Bolt_Dia=44 mm; Bonnet_D=195 mm; Bonnet_D1=390 mm; Bonnet_R=410 mm; Bonnet_dim1=273 mm; Bonnet_dim1_H=76 mm; Bonnet_dim1_H1=597 mm; Bonnet_dim2=137 mm; Bonnet_dim3=102 mm; Bore=250 mm; Bore1=300 mm; Bore2=276 mm; Bore22=304 mm; Centre_D=100 mm; Centre_D1=80 mm; Centre_nut=75 mm; Control_dim1=26 mm; Control_dim2=123 mm; Control_dim3=13 mm  [stored 0.0426509 ft]; Control_dim4=351 mm; Control_dim5=35 mm  [stored 0.114829 ft]; Control_dim6=41 mm; Control_dim7=56 mm; D=325 mm; DN=500 mm; FL_T=27 mm; H3=1160 mm; H33=71 mm; H4=143 mm; L=1250 mm; L3=450 mm; Nut_Dim1=57 mm; Nut_Dim2=10 mm  [stored 0.0328084 ft]; Nut_T=17 mm; Raised_R=30 mm  [stored 0.0984252 ft]; Raised_dis=4 mm  [stored 0.0131234 ft]; Sweep_R=26 mm; Thickness=16 mm; Thickness1=19 mm  [stored 0.062336 ft]; W=448 mm; W1=465 mm; W11=388 mm; W2=465 mm; W22=302 mm; bore2=276 mm; centre=390 mm; dim1=93 mm; dim2=233 mm; nut_dim=195 mm; sweep=41 mm; sweep/2=9 mm  [stored 0.0295276 ft]; sweep1=17 mm; sweep_D=34 mm  [stored 0.111549 ft]; sweep_H=543 mm; sweep_H1=107 mm; sweep_box1=40 mm  [stored 0.131234 ft]; sweep_box2=22 mm
- DN500_PN16 Pilot range ( 0.6 - 6): Actuator_L=209 mm; Actuator_L1=188 mm; Actuator_d=67 mm; Body_H=390 mm; Body_Rib_L=163 mm; Bolt_Dia=44 mm; Bonnet_D=195 mm; Bonnet_D1=390 mm; Bonnet_R=410 mm; Bonnet_dim1=273 mm; Bonnet_dim1_H=76 mm; Bonnet_dim1_H1=597 mm; Bonnet_dim2=137 mm; Bonnet_dim3=102 mm; Bore=250 mm; Bore1=300 mm; Bore2=276 mm; Bore22=304 mm; Centre_D=100 mm; Centre_D1=80 mm; Centre_nut=75 mm; Control_dim1=26 mm; Control_dim2=123 mm; Control_dim3=13 mm  [stored 0.0426509 ft]; Control_dim4=351 mm; Control_dim5=35 mm  [stored 0.114829 ft]; Control_dim6=41 mm; Control_dim7=56 mm; D=325 mm; DN=500 mm; FL_T=27 mm; H3=1160 mm; H33=71 mm; H4=143 mm; L=1250 mm; L3=450 mm; Nut_Dim1=57 mm; Nut_Dim2=10 mm  [stored 0.0328084 ft]; Nut_T=17 mm; Raised_R=30 mm  [stored 0.0984252 ft]; Raised_dis=4 mm  [stored 0.0131234 ft]; Sweep_R=26 mm; Thickness=16 mm; Thickness1=19 mm  [stored 0.062336 ft]; W=448 mm; W1=465 mm; W11=388 mm; W2=465 mm; W22=302 mm; bore2=276 mm; centre=390 mm; dim1=93 mm; dim2=233 mm; nut_dim=195 mm; sweep=41 mm; sweep/2=9 mm  [stored 0.0295276 ft]; sweep1=17 mm; sweep_D=34 mm  [stored 0.111549 ft]; sweep_H=543 mm; sweep_H1=107 mm; sweep_box1=40 mm  [stored 0.131234 ft]; sweep_box2=22 mm
- DN500_PN16 Pilot range ( 5 - 10): Actuator_L=209 mm; Actuator_L1=188 mm; Actuator_d=67 mm; Body_H=390 mm; Body_Rib_L=163 mm; Bolt_Dia=44 mm; Bonnet_D=195 mm; Bonnet_D1=390 mm; Bonnet_R=410 mm; Bonnet_dim1=273 mm; Bonnet_dim1_H=76 mm; Bonnet_dim1_H1=597 mm; Bonnet_dim2=137 mm; Bonnet_dim3=102 mm; Bore=250 mm; Bore1=300 mm; Bore2=276 mm; Bore22=304 mm; Centre_D=100 mm; Centre_D1=80 mm; Centre_nut=75 mm; Control_dim1=26 mm; Control_dim2=123 mm; Control_dim3=13 mm  [stored 0.0426509 ft]; Control_dim4=351 mm; Control_dim5=35 mm  [stored 0.114829 ft]; Control_dim6=41 mm; Control_dim7=56 mm; D=325 mm; DN=500 mm; FL_T=27 mm; H3=1160 mm; H33=71 mm; H4=143 mm; L=1250 mm; L3=450 mm; Nut_Dim1=57 mm; Nut_Dim2=10 mm  [stored 0.0328084 ft]; Nut_T=17 mm; Raised_R=30 mm  [stored 0.0984252 ft]; Raised_dis=4 mm  [stored 0.0131234 ft]; Sweep_R=26 mm; Thickness=16 mm; Thickness1=19 mm  [stored 0.062336 ft]; W=448 mm; W1=465 mm; W11=388 mm; W2=465 mm; W22=302 mm; bore2=276 mm; centre=390 mm; dim1=93 mm; dim2=233 mm; nut_dim=195 mm; sweep=41 mm; sweep/2=9 mm  [stored 0.0295276 ft]; sweep1=17 mm; sweep_D=34 mm  [stored 0.111549 ft]; sweep_H=543 mm; sweep_H1=107 mm; sweep_box1=40 mm  [stored 0.131234 ft]; sweep_box2=22 mm
- DN500_PN16 Pilot range ( 10 - 16): Actuator_L=209 mm; Actuator_L1=188 mm; Actuator_d=67 mm; Body_H=390 mm; Body_Rib_L=163 mm; Bolt_Dia=44 mm; Bonnet_D=195 mm; Bonnet_D1=390 mm; Bonnet_R=410 mm; Bonnet_dim1=273 mm; Bonnet_dim1_H=76 mm; Bonnet_dim1_H1=597 mm; Bonnet_dim2=137 mm; Bonnet_dim3=102 mm; Bore=250 mm; Bore1=300 mm; Bore2=276 mm; Bore22=304 mm; Centre_D=100 mm; Centre_D1=80 mm; Centre_nut=75 mm; Control_dim1=26 mm; Control_dim2=123 mm; Control_dim3=13 mm  [stored 0.0426509 ft]; Control_dim4=351 mm; Control_dim5=35 mm  [stored 0.114829 ft]; Control_dim6=41 mm; Control_dim7=56 mm; D=325 mm; DN=500 mm; FL_T=27 mm; H3=1160 mm; H33=71 mm; H4=143 mm; L=1250 mm; L3=450 mm; Nut_Dim1=57 mm; Nut_Dim2=10 mm  [stored 0.0328084 ft]; Nut_T=17 mm; Raised_R=30 mm  [stored 0.0984252 ft]; Raised_dis=4 mm  [stored 0.0131234 ft]; Sweep_R=26 mm; Thickness=16 mm; Thickness1=19 mm  [stored 0.062336 ft]; W=448 mm; W1=465 mm; W11=388 mm; W2=465 mm; W22=302 mm; bore2=276 mm; centre=390 mm; dim1=93 mm; dim2=233 mm; nut_dim=195 mm; sweep=41 mm; sweep/2=9 mm  [stored 0.0295276 ft]; sweep1=17 mm; sweep_D=34 mm  [stored 0.111549 ft]; sweep_H=543 mm; sweep_H1=107 mm; sweep_box1=40 mm  [stored 0.131234 ft]; sweep_box2=22 mm
- DN500_PN16 Pilot range ( 0.1 - 1): Actuator_L=209 mm; Actuator_L1=188 mm; Actuator_d=67 mm; Body_H=390 mm; Body_Rib_L=163 mm; Bolt_Dia=44 mm; Bonnet_D=195 mm; Bonnet_D1=390 mm; Bonnet_R=410 mm; Bonnet_dim1=273 mm; Bonnet_dim1_H=76 mm; Bonnet_dim1_H1=597 mm; Bonnet_dim2=137 mm; Bonnet_dim3=102 mm; Bore=250 mm; Bore1=300 mm; Bore2=276 mm; Bore22=304 mm; Centre_D=100 mm; Centre_D1=80 mm; Centre_nut=75 mm; Control_dim1=26 mm; Control_dim2=123 mm; Control_dim3=13 mm  [stored 0.0426509 ft]; Control_dim4=351 mm; Control_dim5=35 mm  [stored 0.114829 ft]; Control_dim6=41 mm; Control_dim7=56 mm; D=325 mm; DN=500 mm; FL_T=27 mm; H3=1160 mm; H33=71 mm; H4=143 mm; L=1250 mm; L3=450 mm; Nut_Dim1=57 mm; Nut_Dim2=10 mm  [stored 0.0328084 ft]; Nut_T=17 mm; Raised_R=30 mm  [stored 0.0984252 ft]; Raised_dis=4 mm  [stored 0.0131234 ft]; Sweep_R=26 mm; Thickness=16 mm; Thickness1=19 mm  [stored 0.062336 ft]; W=448 mm; W1=465 mm; W11=388 mm; W2=465 mm; W22=302 mm; bore2=276 mm; centre=390 mm; dim1=93 mm; dim2=233 mm; nut_dim=195 mm; sweep=41 mm; sweep/2=9 mm  [stored 0.0295276 ft]; sweep1=17 mm; sweep_D=34 mm  [stored 0.111549 ft]; sweep_H=543 mm; sweep_H1=107 mm; sweep_box1=40 mm  [stored 0.131234 ft]; sweep_box2=22 mm
- DN600_PN10 Pilot range ( 0.6 - 6): Actuator_L=229 mm; Actuator_L1=206 mm; Actuator_d=80 mm; Body_H=462 mm; Body_Rib_L=193 mm; Bolt_Dia=44 mm; Bonnet_D=231 mm; Bonnet_D1=462 mm; Bonnet_R=485 mm; Bonnet_dim1=323 mm; Bonnet_dim1_H=56 mm; Bonnet_dim1_H1=631 mm; Bonnet_dim2=162 mm; Bonnet_dim3=121 mm; Bore=300 mm; Bore1=360 mm; Bore2=327 mm; Bore22=360 mm; Centre_D=100 mm; Centre_D1=80 mm; Centre_nut=75 mm; Control_dim1=30 mm  [stored 0.0984252 ft]; Control_dim2=146 mm; Control_dim3=15 mm  [stored 0.0492126 ft]; Control_dim4=416 mm; Control_dim5=41 mm; Control_dim6=49 mm; Control_dim7=66 mm; D=385 mm; DN=600 mm; FL_T=30 mm  [stored 0.0984252 ft]; H3=1268 mm; H33=75 mm; H4=151 mm; L=1450 mm; L3=534 mm; Nut_Dim1=57 mm; Nut_Dim2=12 mm  [stored 0.0393701 ft]; Nut_T=20 mm  [stored 0.0656168 ft]; Raised_R=34 mm  [stored 0.111549 ft]; Raised_dis=5 mm  [stored 0.0164042 ft]; Sweep_R=26 mm; Thickness=18 mm  [stored 0.0590551 ft]; Thickness1=22 mm; W=492 mm; W1=509 mm; W11=428 mm; W2=509 mm; W22=331 mm; bore2=327 mm; centre=468 mm; dim1=102 mm; dim2=255 mm; nut_dim=231 mm; sweep=41 mm; sweep/2=9 mm  [stored 0.0295276 ft]; sweep1=17 mm; sweep_D=34 mm  [stored 0.111549 ft]; sweep_H=574 mm; sweep_H1=78 mm; sweep_box1=40 mm  [stored 0.131234 ft]; sweep_box2=22 mm
- DN600_PN10 Pilot range ( 5 - 10): Actuator_L=229 mm; Actuator_L1=206 mm; Actuator_d=80 mm; Body_H=462 mm; Body_Rib_L=193 mm; Bolt_Dia=44 mm; Bonnet_D=231 mm; Bonnet_D1=462 mm; Bonnet_R=485 mm; Bonnet_dim1=323 mm; Bonnet_dim1_H=56 mm; Bonnet_dim1_H1=631 mm; Bonnet_dim2=162 mm; Bonnet_dim3=121 mm; Bore=300 mm; Bore1=360 mm; Bore2=327 mm; Bore22=360 mm; Centre_D=100 mm; Centre_D1=80 mm; Centre_nut=75 mm; Control_dim1=30 mm  [stored 0.0984252 ft]; Control_dim2=146 mm; Control_dim3=15 mm  [stored 0.0492126 ft]; Control_dim4=416 mm; Control_dim5=41 mm; Control_dim6=49 mm; Control_dim7=66 mm; D=385 mm; DN=600 mm; FL_T=30 mm  [stored 0.0984252 ft]; H3=1268 mm; H33=75 mm; H4=151 mm; L=1450 mm; L3=534 mm; Nut_Dim1=57 mm; Nut_Dim2=12 mm  [stored 0.0393701 ft]; Nut_T=20 mm  [stored 0.0656168 ft]; Raised_R=34 mm  [stored 0.111549 ft]; Raised_dis=5 mm  [stored 0.0164042 ft]; Sweep_R=26 mm; Thickness=18 mm  [stored 0.0590551 ft]; Thickness1=22 mm; W=492 mm; W1=509 mm; W11=428 mm; W2=509 mm; W22=331 mm; bore2=327 mm; centre=468 mm; dim1=102 mm; dim2=255 mm; nut_dim=231 mm; sweep=41 mm; sweep/2=9 mm  [stored 0.0295276 ft]; sweep1=17 mm; sweep_D=34 mm  [stored 0.111549 ft]; sweep_H=574 mm; sweep_H1=78 mm; sweep_box1=40 mm  [stored 0.131234 ft]; sweep_box2=22 mm
- DN600_PN10 Pilot range ( 0.1 - 1): Actuator_L=229 mm; Actuator_L1=206 mm; Actuator_d=80 mm; Body_H=462 mm; Body_Rib_L=193 mm; Bolt_Dia=44 mm; Bonnet_D=231 mm; Bonnet_D1=462 mm; Bonnet_R=485 mm; Bonnet_dim1=323 mm; Bonnet_dim1_H=56 mm; Bonnet_dim1_H1=631 mm; Bonnet_dim2=162 mm; Bonnet_dim3=121 mm; Bore=300 mm; Bore1=360 mm; Bore2=327 mm; Bore22=360 mm; Centre_D=100 mm; Centre_D1=80 mm; Centre_nut=75 mm; Control_dim1=30 mm  [stored 0.0984252 ft]; Control_dim2=146 mm; Control_dim3=15 mm  [stored 0.0492126 ft]; Control_dim4=416 mm; Control_dim5=41 mm; Control_dim6=49 mm; Control_dim7=66 mm; D=385 mm; DN=600 mm; FL_T=30 mm  [stored 0.0984252 ft]; H3=1268 mm; H33=75 mm; H4=151 mm; L=1450 mm; L3=534 mm; Nut_Dim1=57 mm; Nut_Dim2=12 mm  [stored 0.0393701 ft]; Nut_T=20 mm  [stored 0.0656168 ft]; Raised_R=34 mm  [stored 0.111549 ft]; Raised_dis=5 mm  [stored 0.0164042 ft]; Sweep_R=26 mm; Thickness=18 mm  [stored 0.0590551 ft]; Thickness1=22 mm; W=492 mm; W1=509 mm; W11=428 mm; W2=509 mm; W22=331 mm; bore2=327 mm; centre=468 mm; dim1=102 mm; dim2=255 mm; nut_dim=231 mm; sweep=41 mm; sweep/2=9 mm  [stored 0.0295276 ft]; sweep1=17 mm; sweep_D=34 mm  [stored 0.111549 ft]; sweep_H=574 mm; sweep_H1=78 mm; sweep_box1=40 mm  [stored 0.131234 ft]; sweep_box2=22 mm
- DN600_PN16 Pilot range ( 0.6 - 6): Actuator_L=229 mm; Actuator_L1=206 mm; Actuator_d=80 mm; Body_H=462 mm; Body_Rib_L=193 mm; Bolt_Dia=44 mm; Bonnet_D=231 mm; Bonnet_D1=462 mm; Bonnet_R=485 mm; Bonnet_dim1=323 mm; Bonnet_dim1_H=56 mm; Bonnet_dim1_H1=631 mm; Bonnet_dim2=162 mm; Bonnet_dim3=121 mm; Bore=300 mm; Bore1=360 mm; Bore2=327 mm; Bore22=360 mm; Centre_D=100 mm; Centre_D1=80 mm; Centre_nut=75 mm; Control_dim1=30 mm  [stored 0.0984252 ft]; Control_dim2=146 mm; Control_dim3=15 mm  [stored 0.0492126 ft]; Control_dim4=416 mm; Control_dim5=41 mm; Control_dim6=49 mm; Control_dim7=66 mm; D=385 mm; DN=600 mm; FL_T=30 mm  [stored 0.0984252 ft]; H3=1268 mm; H33=75 mm; H4=151 mm; L=1450 mm; L3=534 mm; Nut_Dim1=57 mm; Nut_Dim2=12 mm  [stored 0.0393701 ft]; Nut_T=20 mm  [stored 0.0656168 ft]; Raised_R=34 mm  [stored 0.111549 ft]; Raised_dis=5 mm  [stored 0.0164042 ft]; Sweep_R=26 mm; Thickness=18 mm  [stored 0.0590551 ft]; Thickness1=22 mm; W=492 mm; W1=509 mm; W11=428 mm; W2=509 mm; W22=331 mm; bore2=327 mm; centre=468 mm; dim1=102 mm; dim2=255 mm; nut_dim=231 mm; sweep=41 mm; sweep/2=9 mm  [stored 0.0295276 ft]; sweep1=17 mm; sweep_D=34 mm  [stored 0.111549 ft]; sweep_H=574 mm; sweep_H1=78 mm; sweep_box1=40 mm  [stored 0.131234 ft]; sweep_box2=22 mm
- DN600_PN16 Pilot range ( 5 - 10): Actuator_L=229 mm; Actuator_L1=206 mm; Actuator_d=80 mm; Body_H=462 mm; Body_Rib_L=193 mm; Bolt_Dia=44 mm; Bonnet_D=231 mm; Bonnet_D1=462 mm; Bonnet_R=485 mm; Bonnet_dim1=323 mm; Bonnet_dim1_H=56 mm; Bonnet_dim1_H1=631 mm; Bonnet_dim2=162 mm; Bonnet_dim3=121 mm; Bore=300 mm; Bore1=360 mm; Bore2=327 mm; Bore22=360 mm; Centre_D=100 mm; Centre_D1=80 mm; Centre_nut=75 mm; Control_dim1=30 mm  [stored 0.0984252 ft]; Control_dim2=146 mm; Control_dim3=15 mm  [stored 0.0492126 ft]; Control_dim4=416 mm; Control_dim5=41 mm; Control_dim6=49 mm; Control_dim7=66 mm; D=385 mm; DN=600 mm; FL_T=30 mm  [stored 0.0984252 ft]; H3=1268 mm; H33=75 mm; H4=151 mm; L=1450 mm; L3=534 mm; Nut_Dim1=57 mm; Nut_Dim2=12 mm  [stored 0.0393701 ft]; Nut_T=20 mm  [stored 0.0656168 ft]; Raised_R=34 mm  [stored 0.111549 ft]; Raised_dis=5 mm  [stored 0.0164042 ft]; Sweep_R=26 mm; Thickness=18 mm  [stored 0.0590551 ft]; Thickness1=22 mm; W=492 mm; W1=509 mm; W11=428 mm; W2=509 mm; W22=331 mm; bore2=327 mm; centre=468 mm; dim1=102 mm; dim2=255 mm; nut_dim=231 mm; sweep=41 mm; sweep/2=9 mm  [stored 0.0295276 ft]; sweep1=17 mm; sweep_D=34 mm  [stored 0.111549 ft]; sweep_H=574 mm; sweep_H1=78 mm; sweep_box1=40 mm  [stored 0.131234 ft]; sweep_box2=22 mm
- DN600_PN16 Pilot range ( 10 - 16): Actuator_L=229 mm; Actuator_L1=206 mm; Actuator_d=80 mm; Body_H=462 mm; Body_Rib_L=193 mm; Bolt_Dia=44 mm; Bonnet_D=231 mm; Bonnet_D1=462 mm; Bonnet_R=485 mm; Bonnet_dim1=323 mm; Bonnet_dim1_H=56 mm; Bonnet_dim1_H1=631 mm; Bonnet_dim2=162 mm; Bonnet_dim3=121 mm; Bore=300 mm; Bore1=360 mm; Bore2=327 mm; Bore22=360 mm; Centre_D=100 mm; Centre_D1=80 mm; Centre_nut=75 mm; Control_dim1=30 mm  [stored 0.0984252 ft]; Control_dim2=146 mm; Control_dim3=15 mm  [stored 0.0492126 ft]; Control_dim4=416 mm; Control_dim5=41 mm; Control_dim6=49 mm; Control_dim7=66 mm; D=385 mm; DN=600 mm; FL_T=30 mm  [stored 0.0984252 ft]; H3=1268 mm; H33=75 mm; H4=151 mm; L=1450 mm; L3=534 mm; Nut_Dim1=57 mm; Nut_Dim2=12 mm  [stored 0.0393701 ft]; Nut_T=20 mm  [stored 0.0656168 ft]; Raised_R=34 mm  [stored 0.111549 ft]; Raised_dis=5 mm  [stored 0.0164042 ft]; Sweep_R=26 mm; Thickness=18 mm  [stored 0.0590551 ft]; Thickness1=22 mm; W=492 mm; W1=509 mm; W11=428 mm; W2=509 mm; W22=331 mm; bore2=327 mm; centre=468 mm; dim1=102 mm; dim2=255 mm; nut_dim=231 mm; sweep=41 mm; sweep/2=9 mm  [stored 0.0295276 ft]; sweep1=17 mm; sweep_D=34 mm  [stored 0.111549 ft]; sweep_H=574 mm; sweep_H1=78 mm; sweep_box1=40 mm  [stored 0.131234 ft]; sweep_box2=22 mm
- DN600_PN16 Pilot range ( 0.1 - 1): Actuator_L=229 mm; Actuator_L1=206 mm; Actuator_d=80 mm; Body_H=462 mm; Body_Rib_L=193 mm; Bolt_Dia=44 mm; Bonnet_D=231 mm; Bonnet_D1=462 mm; Bonnet_R=485 mm; Bonnet_dim1=323 mm; Bonnet_dim1_H=56 mm; Bonnet_dim1_H1=631 mm; Bonnet_dim2=162 mm; Bonnet_dim3=121 mm; Bore=300 mm; Bore1=360 mm; Bore2=327 mm; Bore22=360 mm; Centre_D=100 mm; Centre_D1=80 mm; Centre_nut=75 mm; Control_dim1=30 mm  [stored 0.0984252 ft]; Control_dim2=146 mm; Control_dim3=15 mm  [stored 0.0492126 ft]; Control_dim4=416 mm; Control_dim5=41 mm; Control_dim6=49 mm; Control_dim7=66 mm; D=385 mm; DN=600 mm; FL_T=30 mm  [stored 0.0984252 ft]; H3=1268 mm; H33=75 mm; H4=151 mm; L=1450 mm; L3=534 mm; Nut_Dim1=57 mm; Nut_Dim2=12 mm  [stored 0.0393701 ft]; Nut_T=20 mm  [stored 0.0656168 ft]; Raised_R=34 mm  [stored 0.111549 ft]; Raised_dis=5 mm  [stored 0.0164042 ft]; Sweep_R=26 mm; Thickness=18 mm  [stored 0.0590551 ft]; Thickness1=22 mm; W=492 mm; W1=509 mm; W11=428 mm; W2=509 mm; W22=331 mm; bore2=327 mm; centre=468 mm; dim1=102 mm; dim2=255 mm; nut_dim=231 mm; sweep=41 mm; sweep/2=9 mm  [stored 0.0295276 ft]; sweep1=17 mm; sweep_D=34 mm  [stored 0.111549 ft]; sweep_H=574 mm; sweep_H1=78 mm; sweep_box1=40 mm  [stored 0.131234 ft]; sweep_box2=22 mm

note: [stored X ft] marks values corroborated as IEEE doubles in the binary element streams (Revit-internal decimal feet)

## geometry (parser evidence)
native form markers: Sweep x6
no freeform markers — native parametric forms only
